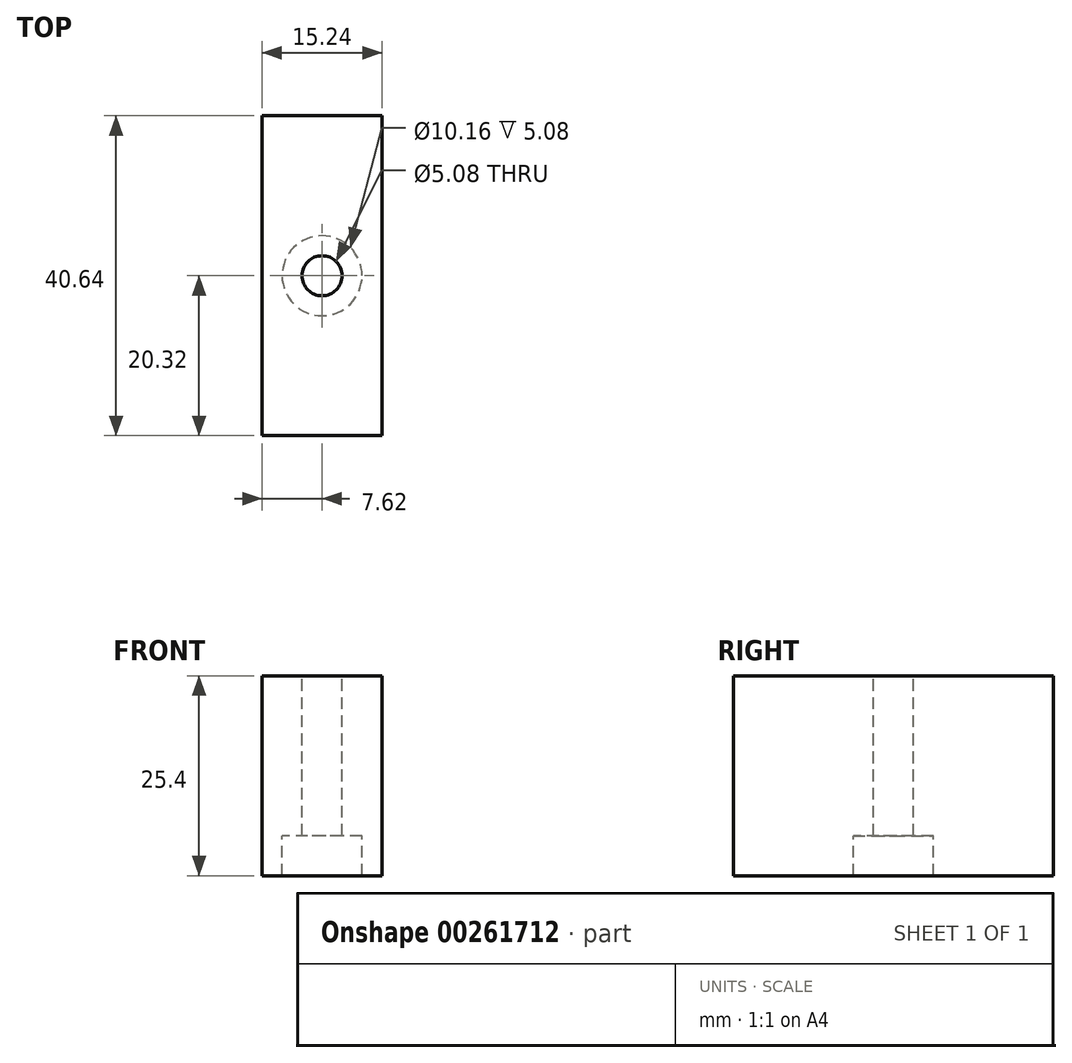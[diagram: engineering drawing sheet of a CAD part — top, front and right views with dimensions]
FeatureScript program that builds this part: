
annotation { "Feature Type Name" : "Feature", "Feature Type Description" : "" }
export const myFeature = defineFeature(function(context is Context, id is Id, definition is map)
    precondition{}
    {
        {
            var Q0;
            Q0=qCreatedBy(makeId("Top.planeOp"),FACE);
            var sketch = newSketch(context, id + "F0", { "sketchPlane" : qUnion([Q0])});
            skLineSegment(sketch, "E0.bottom", {"start": v(0, 0) * mm, "end": v(15.24, 0) * mm});
            skLineSegment(sketch, "E0.top", {"start": v(0, -40.64) * mm, "end": v(15.24, -40.64) * mm});
            skLineSegment(sketch, "E0.left", {"start": v(0, 0) * mm, "end": v(0, -40.64) * mm});
            skLineSegment(sketch, "E0.right", {"start": v(15.24, 0) * mm, "end": v(15.24, -40.64) * mm});
            skCircle(sketch, "E1", {"center": v(7.62, -20.32) * mm, "radius": 2.54 * mm});
            skCircle(sketch, "E2", {"center": v(7.62, -20.32) * mm, "radius": 5.08 * mm});
            skSolve(sketch);
        }
        {
            var Q0;
            Q0 = qSketchRegion(id + "F0", true);
            extrude(context, id + "F1", {"entities" : qUnion([Q0]), "oppositeDirection" : true, "depth" : 25.4 * mm});
        }
        {
            var Q0;
            Q0=makeQuery(id+"F0.imprint","IMPRINT",FACE,{"disambiguationData":[TD([[makeQuery(id+"F0.imprint","IMPRINT",EDGE,{"derivedFrom":sQuery(id+"F0.wireOp",EDGE,"E1")}),-1.0]])]});
            extrude(context, id + "F2", {"entities" : qUnion([Q0]), "operationType" : NewBodyOperationType.ADD, "oppositeDirection" : true, "depth" : 20.32 * mm});
        }
    });
